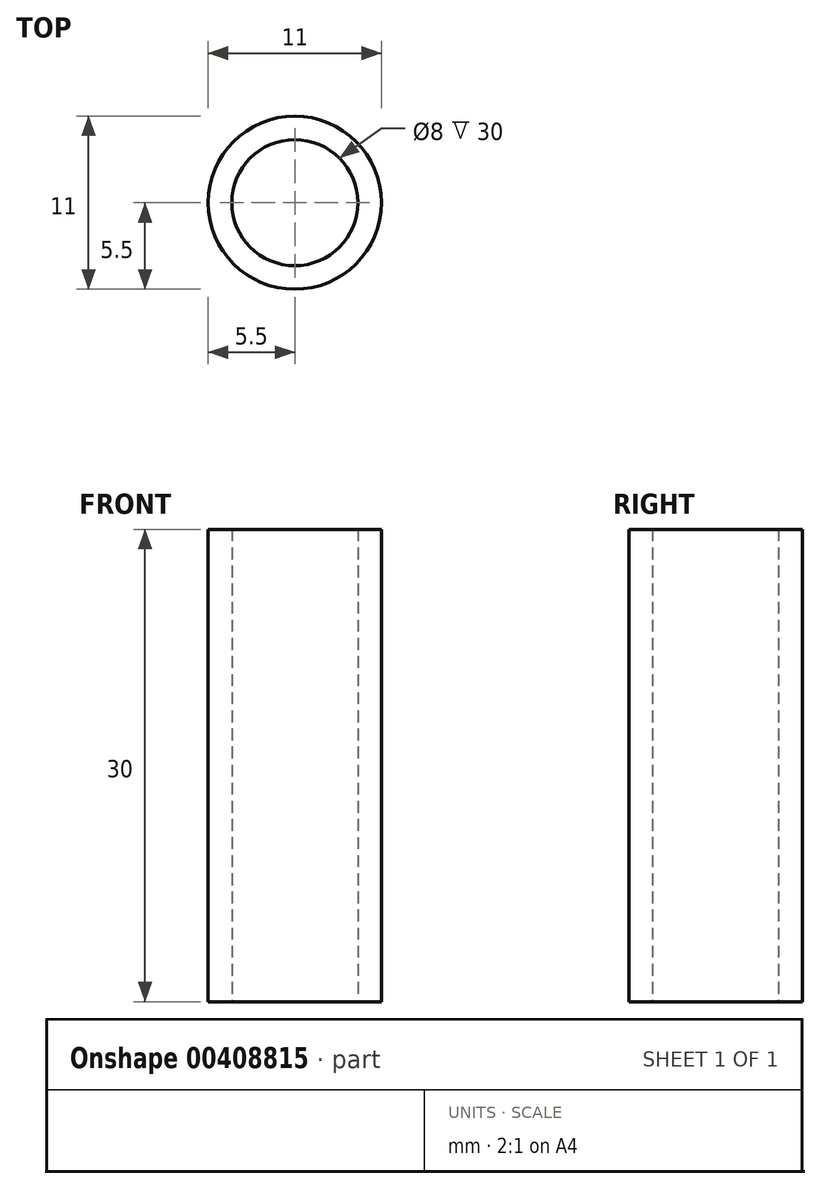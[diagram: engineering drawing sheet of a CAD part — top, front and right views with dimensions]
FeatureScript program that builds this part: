
annotation { "Feature Type Name" : "Feature", "Feature Type Description" : "" }
export const myFeature = defineFeature(function(context is Context, id is Id, definition is map)
    precondition{}
    {
        {
            var Q0;
            Q0=qCreatedBy(makeId("Top.planeOp"),FACE);
            var sketch = newSketch(context, id + "F0", { "sketchPlane" : qUnion([Q0])});
            skCircle(sketch, "E0", {"center": v(0, 0) * mm, "radius": 4 * mm});
            skCircle(sketch, "E1", {"center": v(0, 0) * mm, "radius": 5.5 * mm});
            skSolve(sketch);
        }
        {
            var Q0;
            Q0=makeQuery(id+"F0.imprint","IMPRINT",FACE,{"disambiguationData":[TD([[makeQuery(id+"F0.imprint","IMPRINT",EDGE,{"derivedFrom":sQuery(id+"F0.wireOp",EDGE,"E0")}),-1.0]])]});
            extrude(context, id + "F1", {"entities" : qUnion([Q0]), "endBound" : BoundingType.SYMMETRIC, "depth" : 30 * mm});
        }
    });
